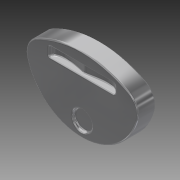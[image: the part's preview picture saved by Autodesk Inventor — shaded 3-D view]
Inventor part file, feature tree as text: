
AUTODESK INVENTOR PART (.ipt)
format: ipt  version: 2011 (Build 150239000, 239)  size: 241,664 bytes
history: native  units: mm (DEFAULTED — no unit token found)
features: fillet x5, extrude x3, sketch x3, chamfer x1, plane x1, mirror x1, reference x1
ambient origin geometry x8: Origin, YZ Plane, XZ Plane, XY Plane, X Axis, Y Axis, Z Axis, Center Point
bodies: Solid1 (feature_tree)
feature tree (15):
  extrude  "Extrusion1"  Depth=3.175mm
  extrude  "Extrusion2"  Depth=0.508mm TaperAngle=0.0deg
  fillet  "Fillet1"  Radius=0.254mm
  chamfer  "Chamfer1"  Distance=0.381mm
  plane  "Work Plane1"
  extrude  "Extrusion3"  Depth=0.7874mm
  mirror  "Mirror1"
  fillet  "Fillet2"  Radius=4.7752mm
  fillet  "Fillet3"  Radius=1.524mm
  fillet  "Fillet4"  Radius=1.524mm
  fillet  "Fillet5"  Radius=0.254mm
  sketch  "Sketch1"  dims[d1=3.175mm d2=0.0mm d3=3.175mm]
  reference  "Reference1"
  sketch  "Sketch2"  dims[d4=3.175mm d5=0.508mm d6=0.0mm d7=0.254mm d8=0.381mm d9=3.175mm]
  sketch  "Sketch3"  dims[d10=3.9624mm d11=0.7874mm d12=4.7752mm d13=1.524mm d14=0.0mm d15=1.524mm d16=0.254mm d17=0.254mm d18=0.508mm d19=0.254mm d20=0.254mm d21=45.0deg]
